# Revit family: REVIT-FLTR-PAIR
name_source: partatom
category: Furniture
units: mm (PartAtom-declared; Revit-internal decimal feet)

## family parameters
Cut with Voids When Loaded = No
Enable Cutting in Views = No
Host = Face
OmniClass Number = 23.40.00.00
OmniClass Title = Equipment and Furnishings
Render Appearance Source = Family Geometry
Room Calculation Point = No
Shared = No

## types (1)
- Miroir 2 LED horizontales 7120-01-01
    Apparent Load = 112 VA
    BIMobject category = Mirrors
    BIMobject category code = sanitary-mirrors
    BIMobject main category = Sanitary
    BIMobject main category code = sanitary
    Brand url = https://www.odf.fr
    Default Elevation = 1600 mm
    Description = Mirror with LED
    Design country = France
    Edition number = 1
    IFC Classification = Furniture
    Keynote = Mirror
    Load Classification = Other
    Manufacturer = ODF
    Manufacturer country = France
    Manufacturer name = ODF Paris
    Masterformat 2014 Code = 08 83 00
    Masterformat 2014 Description = Mirrors
    Material main = Glass
    Material secondary = Aluminium
    Model = 7120 01 01
    NBS Reference Code = 45-55-06
    NBS Reference Description = Bathroom Mirrors
    Nominal height = 650 mm  [stored 2.13255 ft]
    Nominal width = 1980 mm  [stored 6.49606 ft]
    Number of Poles = 1
    OmniClass Code = 23-21 37 13 15
    OmniClass Description = Mirrors
    Power = 36 W
    Product Guid = 8919ff5b-1435-461f-9690-92e34b0786ca
    Product SKU = 7120-01-01
    Product data url = https://bimobject.com
    Product family = Mirrors & Bathroom cabinets
    Product group = Mirrors with integrated lighting
    Product url = https://www.odf.fr
    QR code = http://bimobject.com
    Technical description = https://www.odf.fr
    Type Comments = Mirror
    UNSPSC Code = 301815
    URL = https://www.odf.fr
    Uniclass 1.4 Code = L8732
    Uniclass 1.4 Description = Mirrors
    Uniclass 2.0 Code = PR-45-55-06
    Uniclass 2.0 Description = Bathroom Mirrors
    Uniclass 2015 Code = Pr_25_71_53_06
    Uniclass 2015 Name = Bathroom mirrors
    Uniformat II Code = E20
    Uniformat II Description = FURNISHINGS
    Voltage = 240 V
    Weight Net (Kg) = 0

note: [stored X ft] marks values corroborated as IEEE doubles in the binary element streams (Revit-internal decimal feet)

## geometry (parser evidence)
native form markers: Blend x2, Sweep x7
no freeform markers — native parametric forms only
